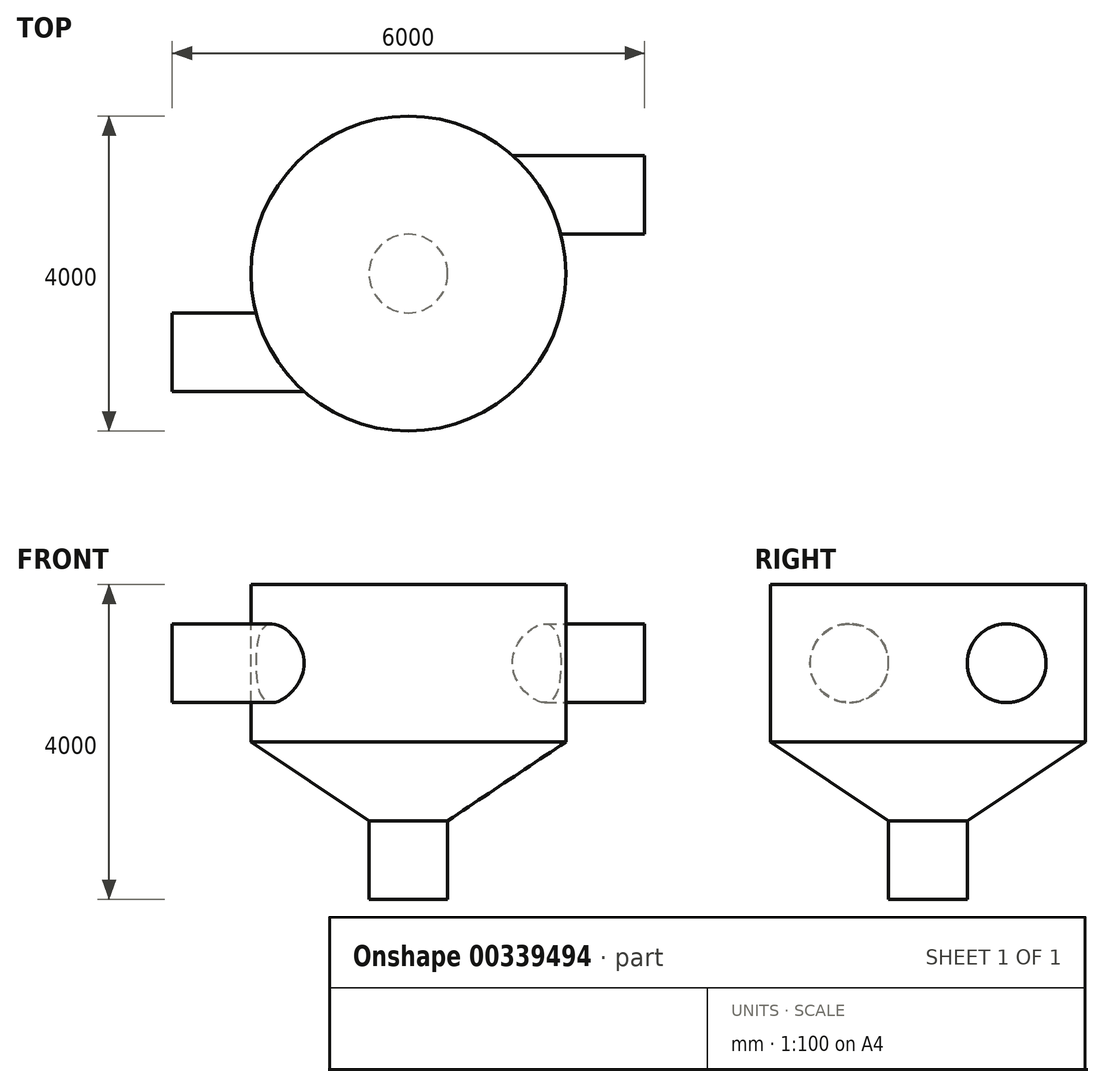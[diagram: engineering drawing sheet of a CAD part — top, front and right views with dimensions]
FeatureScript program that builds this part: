
annotation { "Feature Type Name" : "Feature", "Feature Type Description" : "" }
export const myFeature = defineFeature(function(context is Context, id is Id, definition is map)
    precondition{}
    {
        {
            var Q0;
            Q0=qCreatedBy(makeId("Front.planeOp"),FACE);
            var sketch = newSketch(context, id + "F0", { "sketchPlane" : qUnion([Q0])});
            skLineSegment(sketch, "E0", {"start": v(0, 0) * mm, "end": v(500, 0) * mm});
            skLineSegment(sketch, "E1", {"start": v(500, 0) * mm, "end": v(500, 1000) * mm});
            skLineSegment(sketch, "E2", {"start": v(0, 0) * mm, "end": v(2000, 0) * mm, "construction": true});
            skLineSegment(sketch, "E3", {"start": v(2000, 0) * mm, "end": v(2000, 2000) * mm, "construction": true});
            skLineSegment(sketch, "E4", {"start": v(500, 1000) * mm, "end": v(2000, 2000) * mm});
            skLineSegment(sketch, "E5", {"start": v(2000, 2000) * mm, "end": v(2000, 4000) * mm});
            skLineSegment(sketch, "E6", {"start": v(2000, 4000) * mm, "end": v(0, 4000) * mm});
            skLineSegment(sketch, "E7", {"start": v(0, 4000) * mm, "end": v(0, 0) * mm});
            skSolve(sketch);
        }
        {
            var Q0;
            Q0 = qSketchRegion(id + "F0", true);
            var Q1;
            Q1=sQuery(id+"F0.wireOp",EDGE,"E7");
            revolve(context, id + "F1", {"entities" : qUnion([Q0]), "axis" : qUnion([Q1]), "revolveType" : RevolveType.FULL});
        }
        {
            var Q0;
            Q0=qCreatedBy(makeId("Right.planeOp"),FACE);
            cPlane(context, id + "F2", {"entities" : qUnion([Q0]), "cplaneType" : CPlaneType.OFFSET, "offset" : 3000 * mm, "width" : 150 * mm, "height" : 150 * mm});
        }
        {
            var Q0;
            Q0=qCreatedBy(id+"F2.planeOp",FACE);
            var sketch = newSketch(context, id + "F3", { "sketchPlane" : qUnion([Q0])});
            skLineSegment(sketch, "E8", {"start": v(0, 0) * mm, "end": v(1000, 0) * mm, "construction": true});
            skLineSegment(sketch, "E9", {"start": v(1000, 0) * mm, "end": v(1000, 3000) * mm, "construction": true});
            skCircle(sketch, "E10", {"center": v(1000, 3000) * mm, "radius": 500 * mm});
            skSolve(sketch);
        }
        {
            var Q0;
            Q0 = qSketchRegion(id + "F3", true);
            extrude(context, id + "F4", {"entities" : qUnion([Q0]), "operationType" : NewBodyOperationType.ADD, "endBound" : BoundingType.UP_TO_NEXT, "oppositeDirection" : true, "depth" : 25 * mm});
        }
        {
            var Q0;
            Q0=qCreatedBy(makeId("Right.planeOp"),FACE);
            cPlane(context, id + "F5", {"entities" : qUnion([Q0]), "cplaneType" : CPlaneType.OFFSET, "offset" : 3000 * mm, "oppositeDirection" : true, "width" : 150 * mm, "height" : 150 * mm});
        }
        {
            var Q0;
            Q0=qCreatedBy(id+"F5.planeOp",FACE);
            var sketch = newSketch(context, id + "F6", { "sketchPlane" : qUnion([Q0])});
            skLineSegment(sketch, "E11", {"start": v(0, 0) * mm, "end": v(-1000, 0) * mm, "construction": true});
            skLineSegment(sketch, "E12", {"start": v(-1000, 0) * mm, "end": v(-1000, 3000) * mm, "construction": true});
            skCircle(sketch, "E13", {"center": v(-1000, 3000) * mm, "radius": 500 * mm});
            skSolve(sketch);
        }
        {
            var Q0;
            Q0 = qSketchRegion(id + "F6", true);
            extrude(context, id + "F7", {"entities" : qUnion([Q0]), "operationType" : NewBodyOperationType.ADD, "endBound" : BoundingType.UP_TO_NEXT, "depth" : 25 * mm});
        }
    });
